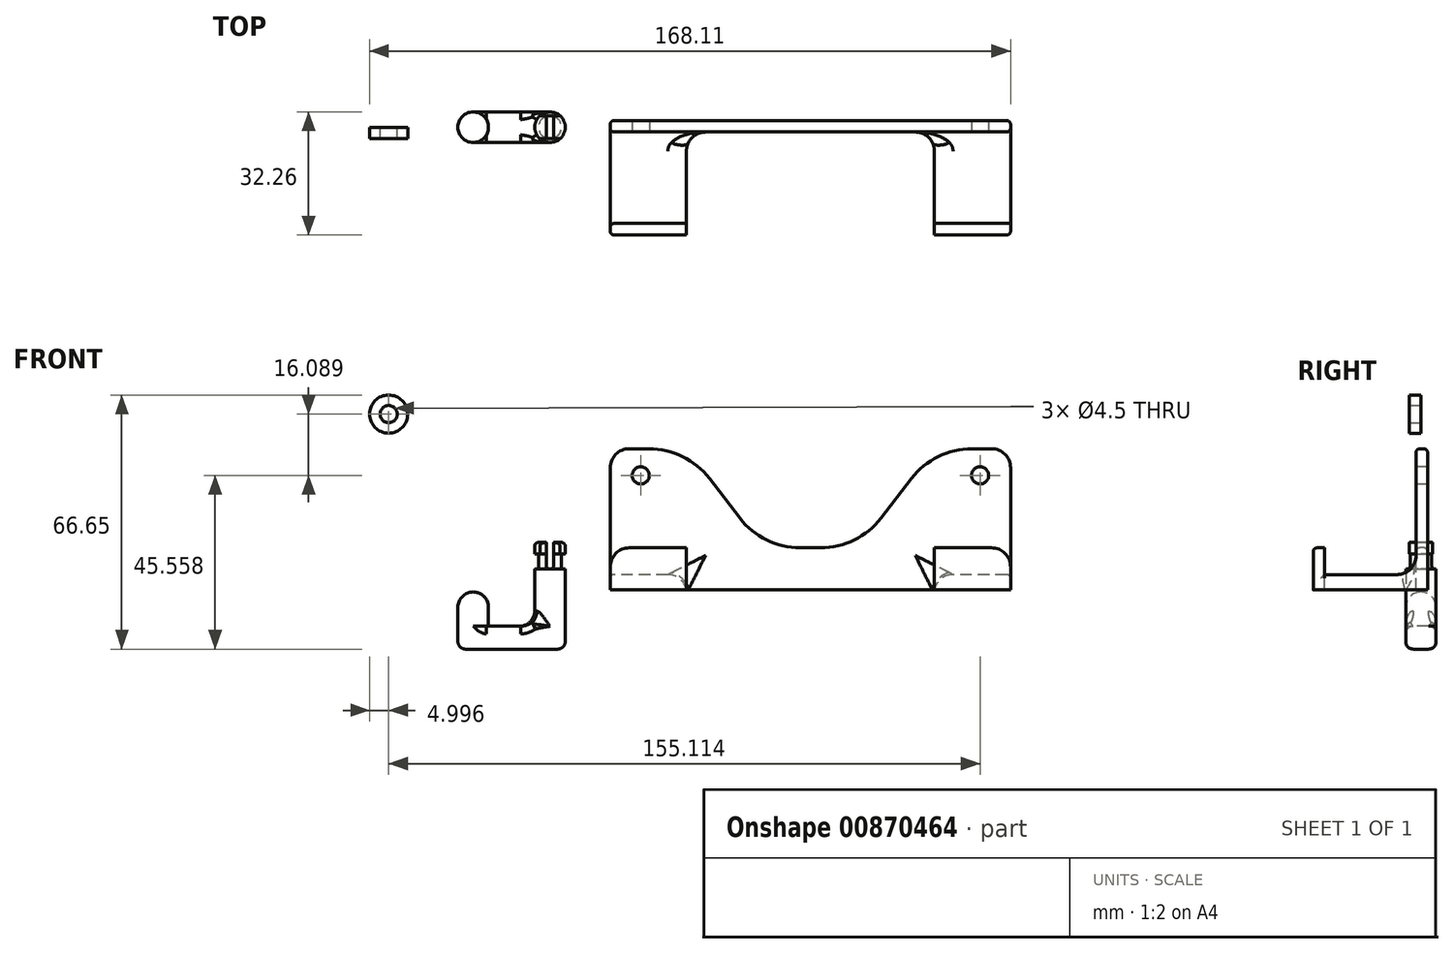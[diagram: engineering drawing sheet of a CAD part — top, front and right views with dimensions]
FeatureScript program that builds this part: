
annotation { "Feature Type Name" : "Feature", "Feature Type Description" : "" }
export const myFeature = defineFeature(function(context is Context, id is Id, definition is map)
    precondition{}
    {
        {
            var Q0;
            Q0=qCreatedBy(makeId("Right.planeOp"),FACE);
            var sketch = newSketch(context, id + "F0", { "sketchPlane" : qUnion([Q0])});
            skLineSegment(sketch, "E0", {"start": v(1.74, 52.56) * mm, "end": v(1.74, 15.56) * mm});
            skLineSegment(sketch, "E1", {"start": v(1.74, 15.56) * mm, "end": v(-28.26, 15.56) * mm});
            skLineSegment(sketch, "E2", {"start": v(-28.26, 15.56) * mm, "end": v(-28.26, 26.56) * mm});
            skLineSegment(sketch, "E3", {"start": v(-28.26, 26.56) * mm, "end": v(-25.26, 26.56) * mm});
            skLineSegment(sketch, "E4", {"start": v(-25.26, 26.56) * mm, "end": v(-25.26, 19.56) * mm});
            skLineSegment(sketch, "E5", {"start": v(-25.26, 19.56) * mm, "end": v(-1.26, 19.56) * mm});
            skLineSegment(sketch, "E6", {"start": v(-1.26, 19.56) * mm, "end": v(-1.26, 52.56) * mm});
            skLineSegment(sketch, "E7", {"start": v(-1.26, 52.56) * mm, "end": v(1.74, 52.56) * mm});
            skSolve(sketch);
        }
        {
            var Q0;
            Q0=makeQuery(id+"F0.imprint","IMPRINT",FACE,{"disambiguationData":[TD([[makeQuery(id+"F0.imprint","IMPRINT",EDGE,{"derivedFrom":sQuery(id+"F0.wireOp",EDGE,"E0")}),-1.0]])]});
            extrude(context, id + "F1", {"entities" : qUnion([Q0]), "depth" : 105 * mm, "offsetDistance" : 25 * mm});
        }
        {
            var Q0;
            Q0=makeQuery(id+"F1.opExtrude","SWEPT_FACE",FACE,{"disambiguationData":[OSD([sQuery(id+"F0.wireOp",EDGE,"E2")])]});
            var sketch = newSketch(context, id + "F2", { "sketchPlane" : qUnion([Q0])});
            skLineSegment(sketch, "E8", {"start": v(52.5, 106.7) * mm, "end": v(52.5, -58.22) * mm, "construction": true});
            skPoint(sketch, "E8.startSnap0", {"position": v(52.5, 26.56) * mm});
            skCircle(sketch, "E9", {"center": v(8, 45.56) * mm, "radius": 2.25 * mm});
            skCircle(sketch, "E10", {"center": v(97, 45.56) * mm, "radius": 2.25 * mm});
            skLineSegment(sketch, "E11.top", {"start": v(20, 15.56) * mm, "end": v(85, 15.56) * mm});
            skLineSegment(sketch, "E11.left", {"start": v(20, 26.56) * mm, "end": v(20, 15.56) * mm});
            skLineSegment(sketch, "E11.right", {"start": v(85, 26.56) * mm, "end": v(85, 15.56) * mm});
            skPoint(sketch, "E12.newPointA", {"position": v(105, 52.56) * mm});
            skPoint(sketch, "E12.newPointB", {"position": v(20, 52.56) * mm});
            skPoint(sketch, "E13.newPointA", {"position": v(40, 26.56) * mm});
            skPoint(sketch, "E14.0.end.orphan", {"position": v(0, 52.56) * mm});
            skLineSegment(sketch, "E15", {"start": v(26, 44.75) * mm, "end": v(34, 34.36) * mm});
            skLineSegment(sketch, "E16", {"start": v(71, 34.36) * mm, "end": v(79, 44.75) * mm});
            skLineSegment(sketch, "E17", {"start": v(85, 52.56) * mm, "end": v(20, 52.56) * mm});
            skLineSegment(sketch, "E18", {"start": v(49.85, 26.56) * mm, "end": v(55.15, 26.56) * mm});
            skArc(sketch, "E19.filletArc", {"start": v(34, 34.36) * mm, "mid": v(41.01, 28.62) * mm, "end": v(49.85, 26.56) * mm});
            skPoint(sketch, "E20.visualSharp", {"position": v(65, 26.56) * mm});
            skArc(sketch, "E20.filletArc", {"start": v(55.15, 26.56) * mm, "mid": v(63.99, 28.62) * mm, "end": v(71, 34.36) * mm});
            skLineSegment(sketch, "E21", {"start": v(10.15, 52.56) * mm, "end": v(0, 52.56) * mm});
            skLineSegment(sketch, "E22", {"start": v(94.85, 52.56) * mm, "end": v(105, 52.56) * mm});
            skArc(sketch, "E23.filletArc", {"start": v(26, 44.75) * mm, "mid": v(18.99, 50.5) * mm, "end": v(10.15, 52.56) * mm});
            skPoint(sketch, "E24.visualSharp", {"position": v(85, 52.56) * mm});
            skArc(sketch, "E24.filletArc", {"start": v(94.85, 52.56) * mm, "mid": v(86.01, 50.5) * mm, "end": v(79, 44.75) * mm});
            skLineSegment(sketch, "E25.0", {"start": v(105, 52.56) * mm, "end": v(0, 52.56) * mm});
            skSolve(sketch);
        }
        {
            var Q0;
            Q0=makeQuery(id+"F2.imprint","IMPRINT",FACE,{"disambiguationData":[TD([[makeQuery(id+"F2.imprint","IMPRINT",EDGE,{"derivedFrom":sQuery(id+"F2.wireOp",EDGE,"E9")}),1.0]])]});
            var Q1;
            Q1=makeQuery(id+"F2.imprint","IMPRINT",FACE,{"disambiguationData":[TD([[makeQuery(id+"F2.imprint","IMPRINT",EDGE,{"derivedFrom":sQuery(id+"F2.wireOp",EDGE,"E10")}),1.0]])]});
            var Q2;
            Q2=makeQuery(id+"F2.imprint","IMPRINT",FACE,{"disambiguationData":[TD([[makeQuery(id+"F2.imprint","IMPRINT",EDGE,{"derivedFrom":sQuery(id+"F2.wireOp",EDGE,"E15")}),1.0]])]});
            extrude(context, id + "F3", {"entities" : qUnion([Q0, Q1, Q2]), "operationType" : NewBodyOperationType.REMOVE, "endBound" : BoundingType.THROUGH_ALL, "oppositeDirection" : true, "depth" : 25 * mm, "offsetDistance" : 25 * mm});
        }
        {
            var Q0;
            Q0=makeQuery(id+"F2.imprint","IMPRINT",FACE,{"disambiguationData":[TD([[makeQuery(id+"F2.imprint","IMPRINT",EDGE,{"derivedFrom":sQuery(id+"F2.wireOp",EDGE,"E11.top")}),-1.0]])]});
            var Q1;
            Q1=makeQuery(id+"F1.opExtrude","SWEPT_FACE",FACE,{"disambiguationData":[OSD([sQuery(id+"F0.wireOp",EDGE,"E6")])]});
            extrude(context, id + "F4", {"entities" : qUnion([Q0]), "operationType" : NewBodyOperationType.REMOVE, "endBound" : BoundingType.UP_TO_SURFACE, "oppositeDirection" : true, "depth" : 25 * mm, "endBoundEntityFace" : qUnion([Q1]), "offsetDistance" : 25 * mm});
        }
        {
            var Q0;
            Q0=makeQuery(id+"F1.opExtrude","CAP_EDGE",EDGE,{"disambiguationData":[OSD([sQuery(id+"F0.wireOp",EDGE,"E7")])],"isStart":true});
            var Q1;
            Q1=makeQuery(id+"F1.opExtrude","CAP_EDGE",EDGE,{"disambiguationData":[OSD([sQuery(id+"F0.wireOp",EDGE,"E7")])],"isStart":false});
            var Q2;
            Q2=makeQuery(id+"F4.boolean.opBoolean","COPY",EDGE,{"derivedFrom":makeQuery(id+"F4.opExtrude","SWEPT_EDGE",EDGE,{"disambiguationData":[OSD([sQuery(id+"F0.wireOp",EDGE,"E2"),sQuery(id+"F0.wireOp",EDGE,"E3"),sQuery(id+"F2.wireOp",EDGE,"E11.right")])]})});
            var Q3;
            Q3=makeQuery(id+"F1.opExtrude","CAP_EDGE",EDGE,{"disambiguationData":[OSD([sQuery(id+"F0.wireOp",EDGE,"E3")])],"isStart":false});
            var Q4;
            Q4=makeQuery(id+"F1.opExtrude","CAP_EDGE",EDGE,{"disambiguationData":[OSD([sQuery(id+"F0.wireOp",EDGE,"E3")])],"isStart":true});
            var Q5;
            Q5=makeQuery(id+"F4.boolean.opBoolean","COPY",EDGE,{"derivedFrom":makeQuery(id+"F4.opExtrude","SWEPT_EDGE",EDGE,{"disambiguationData":[OSD([sQuery(id+"F0.wireOp",EDGE,"E2"),sQuery(id+"F0.wireOp",EDGE,"E3"),sQuery(id+"F2.wireOp",EDGE,"E11.left")])]})});
            var Q6;
            {var subQ0=sQuery(id+"F0.wireOp",EDGE,"E6");var subQ1=sQuery(id+"F2.wireOp",EDGE,"E11.right");var subQ4=sQuery(id+"F0.wireOp",EDGE,"E5");Q6=makeQuery(id+"F4.boolean.opBoolean","SPLIT",EDGE,{"disambiguationData":[TD([makeQuery(id+"F4.opExtrude","SWEPT_FACE",FACE,{"disambiguationData":[OSD([subQ1])]})])],"derivedFrom":makeQuery(id+"F1.opExtrude","SWEPT_EDGE",EDGE,{"disambiguationData":[OSD([subQ4,subQ0])]})});}
            var Q7;
            {var subQ0=sQuery(id+"F0.wireOp",EDGE,"E6");var subQ1=sQuery(id+"F2.wireOp",EDGE,"E11.left");var subQ4=sQuery(id+"F0.wireOp",EDGE,"E5");Q7=makeQuery(id+"F4.boolean.opBoolean","SPLIT",EDGE,{"disambiguationData":[TD([makeQuery(id+"F4.opExtrude","SWEPT_FACE",FACE,{"disambiguationData":[OSD([subQ1])]})])],"derivedFrom":makeQuery(id+"F1.opExtrude","SWEPT_EDGE",EDGE,{"disambiguationData":[OSD([subQ4,subQ0])]})});}
            var Q8;
            Q8=makeQuery(id+"F4.boolean.opBoolean","COPY",EDGE,{"derivedFrom":makeQuery(id+"F4.opExtrude","CAP_EDGE",EDGE,{"disambiguationData":[OSD([sQuery(id+"F2.wireOp",EDGE,"E11.right")])],"isStart":false})});
            var Q9;
            Q9=makeQuery(id+"F4.boolean.opBoolean","COPY",EDGE,{"derivedFrom":makeQuery(id+"F4.opExtrude","CAP_EDGE",EDGE,{"disambiguationData":[OSD([sQuery(id+"F2.wireOp",EDGE,"E11.left")])],"isStart":false})});
            fillet(context, id + "F5", {"entities" : qUnion([Q0, Q1, Q2, Q3, Q4, Q5, Q6, Q7, Q8, Q9]), "radius" : 5 * mm, "tangentPropagation" : true, "allowEdgeOverflow" : false});
        }
        {
            var Q0;
            Q0=makeQuery(id+"F4.boolean.opBoolean","INTERSECT",EDGE,{"derivedFrom":[makeQuery(id+"F1.opExtrude","SWEPT_FACE",FACE,{"disambiguationData":[OSD([sQuery(id+"F0.wireOp",EDGE,"E5")])]}),makeQuery(id+"F4.opExtrude","SWEPT_FACE",FACE,{"disambiguationData":[OSD([sQuery(id+"F2.wireOp",EDGE,"E11.right")])]})]});
            var Q1;
            Q1=makeQuery(id+"F4.boolean.opBoolean","INTERSECT",EDGE,{"derivedFrom":[makeQuery(id+"F1.opExtrude","SWEPT_FACE",FACE,{"disambiguationData":[OSD([sQuery(id+"F0.wireOp",EDGE,"E5")])]}),makeQuery(id+"F4.opExtrude","SWEPT_FACE",FACE,{"disambiguationData":[OSD([sQuery(id+"F2.wireOp",EDGE,"E11.left")])]})]});
            fillet(context, id + "F6", {"entities" : qUnion([Q0, Q1]), "radius" : 5 * mm, "tangentPropagation" : true, "allowEdgeOverflow" : false});
        }
        {
            var Q0;
            Q0=makeQuery(id+"F3.boolean.opBoolean","INTERSECT",EDGE,{"derivedFrom":[makeQuery(id+"F1.opExtrude","SWEPT_FACE",FACE,{"disambiguationData":[OSD([sQuery(id+"F0.wireOp",EDGE,"E6")])]}),makeQuery(id+"F3.opExtrude","SWEPT_FACE",FACE,{"disambiguationData":[OSD([sQuery(id+"F2.wireOp",EDGE,"E18")])]})]});
            var Q1;
            Q1=makeQuery(id+"F3.boolean.opBoolean","INTERSECT",EDGE,{"derivedFrom":[makeQuery(id+"F1.opExtrude","SWEPT_FACE",FACE,{"disambiguationData":[OSD([sQuery(id+"F0.wireOp",EDGE,"E0")])]}),makeQuery(id+"F3.opExtrude","SWEPT_FACE",FACE,{"disambiguationData":[OSD([sQuery(id+"F2.wireOp",EDGE,"E18")])]})]});
            var Q2;
            {var subQ0=sQuery(id+"F0.wireOp",EDGE,"E4");var subQ1=sQuery(id+"F0.wireOp",EDGE,"E3");Q2=makeQuery(id+"F4.boolean.opBoolean","SPLIT",EDGE,{"disambiguationData":[TD([makeQuery(id+"F4.opExtrude","SWEPT_FACE",FACE,{"disambiguationData":[OSD([sQuery(id+"F2.wireOp",EDGE,"E11.left")])]})])],"derivedFrom":makeQuery(id+"F1.opExtrude","SWEPT_EDGE",EDGE,{"disambiguationData":[OSD([subQ1,subQ0])]})});}
            var Q3;
            {var subQ0=sQuery(id+"F0.wireOp",EDGE,"E3");var subQ1=sQuery(id+"F0.wireOp",EDGE,"E2");Q3=makeQuery(id+"F4.boolean.opBoolean","SPLIT",EDGE,{"disambiguationData":[TD([makeQuery(id+"F4.opExtrude","SWEPT_FACE",FACE,{"disambiguationData":[OSD([sQuery(id+"F2.wireOp",EDGE,"E11.left")])]})])],"derivedFrom":makeQuery(id+"F1.opExtrude","SWEPT_EDGE",EDGE,{"disambiguationData":[OSD([subQ1,subQ0])]})});}
            var Q4;
            {var subQ0=sQuery(id+"F0.wireOp",EDGE,"E3");var subQ1=sQuery(id+"F0.wireOp",EDGE,"E2");Q4=makeQuery(id+"F4.boolean.opBoolean","SPLIT",EDGE,{"disambiguationData":[TD([makeQuery(id+"F4.opExtrude","SWEPT_FACE",FACE,{"disambiguationData":[OSD([sQuery(id+"F2.wireOp",EDGE,"E11.right")])]})])],"derivedFrom":makeQuery(id+"F1.opExtrude","SWEPT_EDGE",EDGE,{"disambiguationData":[OSD([subQ1,subQ0])]})});}
            var Q5;
            {var subQ1=sQuery(id+"F0.wireOp",EDGE,"E4");var subQ2=sQuery(id+"F0.wireOp",EDGE,"E3");var subQ3=sQuery(id+"F0.wireOp",EDGE,"E2");var subQ4=sQuery(id+"F2.wireOp",EDGE,"E11.right");Q5=makeQuery(id+"F5.opFillet","BLEND_EDGE",EDGE,{"blendedFrom":[makeQuery(id+"F4.boolean.opBoolean","COPY",EDGE,{"derivedFrom":makeQuery(id+"F4.opExtrude","SWEPT_EDGE",EDGE,{"disambiguationData":[OSD([subQ3,subQ2,subQ4])]})}),makeQuery(id+"F4.boolean.opBoolean","SPLIT",FACE,{"disambiguationData":[TD([makeQuery(id+"F4.opExtrude","SWEPT_FACE",FACE,{"disambiguationData":[OSD([subQ4])]})])],"derivedFrom":makeQuery(id+"F1.opExtrude","SWEPT_FACE",FACE,{"disambiguationData":[OSD([subQ1])]})})],"blendedInto":[makeQuery(id+"F4.boolean.opBoolean","SPLIT",FACE,{"disambiguationData":[TD([makeQuery(id+"F4.opExtrude","SWEPT_FACE",FACE,{"disambiguationData":[OSD([subQ4])]})])],"derivedFrom":makeQuery(id+"F1.opExtrude","SWEPT_FACE",FACE,{"disambiguationData":[OSD([subQ1])]})})]});}
            fillet(context, id + "F7", {"entities" : qUnion([Q0, Q1, Q2, Q3, Q4, Q5]), "radius" : 1 * mm, "tangentPropagation" : true, "allowEdgeOverflow" : false});
        }
        {
            var Q0;
            Q0=qCreatedBy(makeId("Top.planeOp"),FACE);
            var sketch = newSketch(context, id + "F8", { "sketchPlane" : qUnion([Q0])});
            skCircle(sketch, "E26", {"center": v(-15.8, 0) * mm, "radius": 4 * mm});
            skCircle(sketch, "E27", {"center": v(-35.94, 0) * mm, "radius": 4 * mm});
            skLineSegment(sketch, "E28", {"start": v(-35.94, -4) * mm, "end": v(-15.8, -4) * mm});
            skLineSegment(sketch, "E29", {"start": v(-15.8, 4) * mm, "end": v(-35.94, 4) * mm});
            skCircle(sketch, "E30", {"center": v(-15.8, 0) * mm, "radius": 3 * mm});
            skSolve(sketch);
        }
        {
            var Q0;
            {var subQ0=sQuery(id+"F8.wireOp",EDGE,"E27");var subQ1=makeQuery(id+"F8.imprint","INTERSECT",VERTEX,{"derivedFrom":[subQ0,sQuery(id+"F8.wireOp",EDGE,"E28")]});Q0=makeQuery(id+"F8.imprint","IMPRINT",FACE,{"disambiguationData":[TD([[makeQuery(id+"F8.imprint","IMPRINT",EDGE,{"disambiguationData":[TD([[subQ1,1.0]])],"derivedFrom":subQ0}),1.0]])]});}
            extrude(context, id + "F9", {"entities" : qUnion([Q0]), "depth" : 15 * mm, "offsetDistance" : 25 * mm});
        }
        {
            var Q0;
            Q0=makeQuery(id+"F8.imprint","IMPRINT",FACE,{"disambiguationData":[TD([[makeQuery(id+"F8.imprint","IMPRINT",EDGE,{"derivedFrom":sQuery(id+"F8.wireOp",EDGE,"E30")}),1.0]])]});
            var Q1;
            Q1=makeQuery(id+"F8.imprint","IMPRINT",FACE,{"disambiguationData":[TD([[makeQuery(id+"F8.imprint","IMPRINT",EDGE,{"derivedFrom":sQuery(id+"F8.wireOp",EDGE,"E30")}),-1.0]])]});
            var Q2;
            {var subQ0=sQuery(id+"F8.wireOp",EDGE,"E28");Q2=makeQuery(id+"F8.imprint","IMPRINT",FACE,{"disambiguationData":[TD([[makeQuery(id+"F8.imprint","IMPRINT",EDGE,{"derivedFrom":subQ0}),1.0]])]});}
            extrude(context, id + "F10", {"entities" : qUnion([Q0, Q1, Q2]), "operationType" : NewBodyOperationType.ADD, "depth" : 6 * mm, "offsetDistance" : 25 * mm});
        }
        {
            var Q0;
            Q0=makeQuery(id+"F8.imprint","IMPRINT",FACE,{"disambiguationData":[TD([[makeQuery(id+"F8.imprint","IMPRINT",EDGE,{"derivedFrom":sQuery(id+"F8.wireOp",EDGE,"E30")}),1.0]])]});
            var Q1;
            Q1=makeQuery(id+"F8.imprint","IMPRINT",FACE,{"disambiguationData":[TD([[makeQuery(id+"F8.imprint","IMPRINT",EDGE,{"derivedFrom":sQuery(id+"F8.wireOp",EDGE,"E30")}),-1.0]])]});
            extrude(context, id + "F11", {"entities" : qUnion([Q0, Q1]), "operationType" : NewBodyOperationType.ADD, "depth" : 28 * mm, "offsetDistance" : 25 * mm});
        }
        {
            var Q0;
            Q0=makeQuery(id+"F8.imprint","IMPRINT",FACE,{"disambiguationData":[TD([[makeQuery(id+"F8.imprint","IMPRINT",EDGE,{"derivedFrom":sQuery(id+"F8.wireOp",EDGE,"E30")}),-1.0]])]});
            extrude(context, id + "F12", {"entities" : qUnion([Q0]), "operationType" : NewBodyOperationType.REMOVE, "depth" : 25 * mm, "offsetDistance" : 25 * mm, "hasSecondDirection" : true, "secondDirectionOppositeDirection" : false, "secondDirectionDepth" : 21 * mm});
        }
        {
            var Q0;
            Q0=makeQuery(id+"F11.opExtrude","CAP_FACE",FACE,{"disambiguationData":[OSD([sQuery(id+"F8.wireOp",EDGE,"E26")])],"isStart":false});
            var sketch = newSketch(context, id + "F13", { "sketchPlane" : qUnion([Q0])});
            skLineSegment(sketch, "E31", {"start": v(-15.8, 29.3) * mm, "end": v(-15.8, -9.23) * mm, "construction": true});
            skLineSegment(sketch, "E32", {"start": v(-8.26, 0) * mm, "end": v(-53.8, 0) * mm, "construction": true});
            skLineSegment(sketch, "E33.bottom", {"start": v(-16.8, 6.08) * mm, "end": v(-14.8, 6.08) * mm});
            skLineSegment(sketch, "E33.top", {"start": v(-16.8, -7.23) * mm, "end": v(-14.8, -7.23) * mm});
            skLineSegment(sketch, "E33.left", {"start": v(-16.8, 6.08) * mm, "end": v(-16.8, -7.23) * mm});
            skLineSegment(sketch, "E33.right", {"start": v(-14.8, 6.08) * mm, "end": v(-14.8, -7.23) * mm});
            skLineSegment(sketch, "E34.bottom", {"start": v(-21.19, 4.55) * mm, "end": v(-9.3, 4.55) * mm});
            skLineSegment(sketch, "E34.top", {"start": v(-21.19, 3) * mm, "end": v(-9.3, 3) * mm});
            skLineSegment(sketch, "E34.left", {"start": v(-21.19, 4.55) * mm, "end": v(-21.19, 3) * mm});
            skLineSegment(sketch, "E34.right", {"start": v(-9.3, 4.55) * mm, "end": v(-9.3, 3) * mm});
            skLineSegment(sketch, "E35.bottom", {"start": v(-21.19, -6.06) * mm, "end": v(-9.07, -6.06) * mm});
            skLineSegment(sketch, "E35.top", {"start": v(-21.19, -3) * mm, "end": v(-9.07, -3) * mm});
            skLineSegment(sketch, "E35.left", {"start": v(-21.19, -6.06) * mm, "end": v(-21.19, -3) * mm});
            skLineSegment(sketch, "E35.right", {"start": v(-9.07, -6.06) * mm, "end": v(-9.07, -3) * mm});
            skSolve(sketch);
        }
        {
            var Q0;
            {var subQ0=sQuery(id+"F13.wireOp",EDGE,"ln6uyzeO-vsmx-rn3P-acM0-f8EmxYZYzspw.left");var subQ1=sQuery(id+"F13.wireOp",EDGE,"qbeKx2qP-LrLk-Yy0b-7lcU-67xgwiWYBIU2.bottom");var subQ2=makeQuery(id+"F13.imprint","INTERSECT",VERTEX,{"derivedFrom":[subQ1,subQ0]});Q0=makeQuery(id+"F13.imprint","IMPRINT",FACE,{"disambiguationData":[TD([[makeQuery(id+"F13.imprint","IMPRINT",EDGE,{"disambiguationData":[TD([[subQ2,-1.0]])],"derivedFrom":subQ1}),1.0]])]});}
            var Q1;
            {var subQ0=sQuery(id+"F13.wireOp",EDGE,"UMEJGvHE-ukJ3-Tcu8-njH4-oKaGY4YRu2tl.left");var subQ1=sQuery(id+"F13.wireOp",EDGE,"qbeKx2qP-LrLk-Yy0b-7lcU-67xgwiWYBIU2.bottom");var subQ2=makeQuery(id+"F13.imprint","INTERSECT",VERTEX,{"derivedFrom":[subQ1,subQ0]});Q1=makeQuery(id+"F13.imprint","IMPRINT",FACE,{"disambiguationData":[TD([[makeQuery(id+"F13.imprint","IMPRINT",EDGE,{"disambiguationData":[TD([[subQ2,-1.0]])],"derivedFrom":subQ1}),1.0]])]});}
            var Q2;
            {var subQ0=sQuery(id+"F13.wireOp",EDGE,"ln6uyzeO-vsmx-rn3P-acM0-f8EmxYZYzspw.left");var subQ1=sQuery(id+"F13.wireOp",EDGE,"qbeKx2qP-LrLk-Yy0b-7lcU-67xgwiWYBIU2.bottom");var subQ2=makeQuery(id+"F13.imprint","INTERSECT",VERTEX,{"derivedFrom":[subQ1,subQ0]});Q2=makeQuery(id+"F13.imprint","IMPRINT",FACE,{"disambiguationData":[TD([[makeQuery(id+"F13.imprint","IMPRINT",EDGE,{"disambiguationData":[TD([[subQ2,1.0]])],"derivedFrom":subQ1}),1.0]])]});}
            var Q3;
            {var subQ0=sQuery(id+"F13.wireOp",EDGE,"E34.top");var subQ1=sQuery(id+"F13.wireOp",EDGE,"E33.left");var subQ2=makeQuery(id+"F13.imprint","INTERSECT",VERTEX,{"derivedFrom":[subQ1,subQ0]});Q3=makeQuery(id+"F13.imprint","IMPRINT",FACE,{"disambiguationData":[TD([[makeQuery(id+"F13.imprint","IMPRINT",EDGE,{"disambiguationData":[TD([[subQ2,1.0]])],"derivedFrom":subQ1}),1.0]])]});}
            var Q4;
            {var subQ0=sQuery(id+"F13.wireOp",EDGE,"E34.top");var subQ1=sQuery(id+"F13.wireOp",EDGE,"E33.left");var subQ2=makeQuery(id+"F13.imprint","INTERSECT",VERTEX,{"derivedFrom":[subQ1,subQ0]});Q4=makeQuery(id+"F13.imprint","IMPRINT",FACE,{"disambiguationData":[TD([[makeQuery(id+"F13.imprint","IMPRINT",EDGE,{"disambiguationData":[TD([[subQ2,-1.0]])],"derivedFrom":subQ1}),1.0]])]});}
            var Q5;
            {var subQ0=sQuery(id+"F13.wireOp",EDGE,"E35.top");var subQ1=sQuery(id+"F13.wireOp",EDGE,"E33.left");var subQ2=makeQuery(id+"F13.imprint","INTERSECT",VERTEX,{"derivedFrom":[subQ1,subQ0]});Q5=makeQuery(id+"F13.imprint","IMPRINT",FACE,{"disambiguationData":[TD([[makeQuery(id+"F13.imprint","IMPRINT",EDGE,{"disambiguationData":[TD([[subQ2,-1.0]])],"derivedFrom":subQ1}),1.0]])]});}
            extrude(context, id + "F14", {"entities" : qUnion([Q0, Q1, Q2, Q3, Q4, Q5]), "operationType" : NewBodyOperationType.REMOVE, "oppositeDirection" : true, "depth" : 7 * mm, "offsetDistance" : 25 * mm});
        }
        {
            var Q0;
            {var subQ1=sQuery(id+"F13.wireOp",EDGE,"qbeKx2qP-LrLk-Yy0b-7lcU-67xgwiWYBIU2.left");Q0=makeQuery(id+"F13.imprint","IMPRINT",FACE,{"disambiguationData":[TD([[makeQuery(id+"F13.imprint","IMPRINT",EDGE,{"derivedFrom":subQ1}),1.0]])]});}
            var Q1;
            {var subQ0=sQuery(id+"F13.wireOp",EDGE,"UMEJGvHE-ukJ3-Tcu8-njH4-oKaGY4YRu2tl.left");var subQ1=sQuery(id+"F13.wireOp",EDGE,"qbeKx2qP-LrLk-Yy0b-7lcU-67xgwiWYBIU2.top");var subQ2=makeQuery(id+"F13.imprint","INTERSECT",VERTEX,{"derivedFrom":[subQ1,subQ0]});Q1=makeQuery(id+"F13.imprint","IMPRINT",FACE,{"disambiguationData":[TD([[makeQuery(id+"F13.imprint","IMPRINT",EDGE,{"disambiguationData":[TD([[subQ2,-1.0]])],"derivedFrom":subQ1}),1.0]])]});}
            var Q2;
            {var subQ0=sQuery(id+"F13.wireOp",EDGE,"E34.top");var subQ1=sQuery(id+"F13.wireOp",EDGE,"E33.left");var subQ2=makeQuery(id+"F13.imprint","INTERSECT",VERTEX,{"derivedFrom":[subQ1,subQ0]});Q2=makeQuery(id+"F13.imprint","IMPRINT",FACE,{"disambiguationData":[TD([[makeQuery(id+"F13.imprint","IMPRINT",EDGE,{"disambiguationData":[TD([[subQ2,1.0]])],"derivedFrom":subQ1}),-1.0]])]});}
            var Q3;
            {var subQ0=sQuery(id+"F13.wireOp",EDGE,"E34.top");var subQ1=sQuery(id+"F13.wireOp",EDGE,"E33.right");var subQ2=makeQuery(id+"F13.imprint","INTERSECT",VERTEX,{"derivedFrom":[subQ1,subQ0]});Q3=makeQuery(id+"F13.imprint","IMPRINT",FACE,{"disambiguationData":[TD([[makeQuery(id+"F13.imprint","IMPRINT",EDGE,{"disambiguationData":[TD([[subQ2,1.0]])],"derivedFrom":subQ1}),1.0]])]});}
            var Q4;
            {var subQ0=sQuery(id+"F13.wireOp",EDGE,"E35.top");var subQ1=sQuery(id+"F13.wireOp",EDGE,"E33.left");var subQ2=makeQuery(id+"F13.imprint","INTERSECT",VERTEX,{"derivedFrom":[subQ1,subQ0]});Q4=makeQuery(id+"F13.imprint","IMPRINT",FACE,{"disambiguationData":[TD([[makeQuery(id+"F13.imprint","IMPRINT",EDGE,{"disambiguationData":[TD([[subQ2,-1.0]])],"derivedFrom":subQ1}),-1.0]])]});}
            var Q5;
            {var subQ0=sQuery(id+"F13.wireOp",EDGE,"E35.top");var subQ1=sQuery(id+"F13.wireOp",EDGE,"E33.right");var subQ2=makeQuery(id+"F13.imprint","INTERSECT",VERTEX,{"derivedFrom":[subQ1,subQ0]});Q5=makeQuery(id+"F13.imprint","IMPRINT",FACE,{"disambiguationData":[TD([[makeQuery(id+"F13.imprint","IMPRINT",EDGE,{"disambiguationData":[TD([[subQ2,-1.0]])],"derivedFrom":subQ1}),1.0]])]});}
            var Q6;
            {var subQ0=sQuery(id+"F13.wireOp",EDGE,"E33.bottom");Q6=makeQuery(id+"F13.imprint","IMPRINT",FACE,{"disambiguationData":[TD([[makeQuery(id+"F13.imprint","IMPRINT",EDGE,{"derivedFrom":subQ0}),-1.0]])]});}
            extrude(context, id + "F15", {"entities" : qUnion([Q0, Q1, Q2, Q3, Q4, Q5, Q6]), "operationType" : NewBodyOperationType.REMOVE, "oppositeDirection" : true, "depth" : 5 * mm, "offsetDistance" : 25 * mm});
        }
        {
            var Q0;
            Q0=makeQuery(id+"F9.opExtrude","CAP_EDGE",EDGE,{"disambiguationData":[OSD([sQuery(id+"F8.wireOp",EDGE,"E27")])],"isStart":false});
            var Q1;
            Q1=makeQuery(id+"F10.opExtrude","CAP_EDGE",EDGE,{"disambiguationData":[OSD([sQuery(id+"F8.wireOp",EDGE,"E27")])],"isStart":false});
            var Q2;
            {var subQ0=sQuery(id+"F8.wireOp",EDGE,"E26");Q2=makeQuery(id+"F11.boolean.opBoolean","INTERSECT",EDGE,{"derivedFrom":[makeQuery(id+"F10.opExtrude","CAP_FACE",FACE,{"disambiguationData":[OSD([subQ0,sQuery(id+"F8.wireOp",EDGE,"E27"),sQuery(id+"F8.wireOp",EDGE,"E28"),sQuery(id+"F8.wireOp",EDGE,"E29")])],"isStart":false}),makeQuery(id+"F11.opExtrude","SWEPT_FACE",FACE,{"disambiguationData":[OSD([subQ0])]})]});}
            fillet(context, id + "F16", {"entities" : qUnion([Q0, Q1, Q2]), "radius" : 4 * mm, "tangentPropagation" : true, "allowEdgeOverflow" : false});
        }
        {
            var Q0;
            {var subQ0=sQuery(id+"F8.wireOp",EDGE,"E26");Q0=makeQuery(id+"F14.boolean.opBoolean","SPLIT",EDGE,{"disambiguationData":[TD([makeQuery(id+"F14.opExtrude","SWEPT_FACE",FACE,{"disambiguationData":[OSD([sQuery(id+"F13.wireOp",EDGE,"J1QhrFvL-nhcP-Zsf0-0vtz-GyqxPvx9N3jh.left")])]})])],"derivedFrom":makeQuery(id+"F11.opExtrude","CAP_EDGE",EDGE,{"disambiguationData":[OSD([subQ0])],"isStart":false})});}
            var Q1;
            {var subQ0=sQuery(id+"F8.wireOp",EDGE,"E26");Q1=makeQuery(id+"F14.boolean.opBoolean","SPLIT",EDGE,{"disambiguationData":[TD([makeQuery(id+"F14.opExtrude","SWEPT_FACE",FACE,{"disambiguationData":[OSD([sQuery(id+"F13.wireOp",EDGE,"J1QhrFvL-nhcP-Zsf0-0vtz-GyqxPvx9N3jh.right")])]})])],"derivedFrom":makeQuery(id+"F11.opExtrude","CAP_EDGE",EDGE,{"disambiguationData":[OSD([subQ0])],"isStart":false})});}
            var Q2;
            Q2=makeQuery(id+"F10.opExtrude","CAP_EDGE",EDGE,{"disambiguationData":[OSD([sQuery(id+"F8.wireOp",EDGE,"E28")])],"isStart":false});
            var Q3;
            Q3=makeQuery(id+"F10.opExtrude","CAP_EDGE",EDGE,{"disambiguationData":[OSD([sQuery(id+"F8.wireOp",EDGE,"E29")])],"isStart":false});
            var Q4;
            {var subQ0=sQuery(id+"F8.wireOp",EDGE,"E27");Q4=makeQuery(id+"F10.boolean.opBoolean","MERGE",FACE,{"derivedFrom":[makeQuery(id+"F9.opExtrude","CAP_FACE",FACE,{"disambiguationData":[OSD([subQ0])],"isStart":true}),makeQuery(id+"F10.opExtrude","CAP_FACE",FACE,{"disambiguationData":[OSD([sQuery(id+"F8.wireOp",EDGE,"E26"),subQ0,sQuery(id+"F8.wireOp",EDGE,"E28"),sQuery(id+"F8.wireOp",EDGE,"E29")])],"isStart":true})]});}
            fillet(context, id + "F17", {"entities" : qUnion([Q0, Q1, Q2, Q3, Q4]), "radius" : 2 * mm, "tangentPropagation" : true, "allowEdgeOverflow" : false});
        }
        {
            var Q0;
            {var subQ0=sQuery(id+"F8.wireOp",EDGE,"E26");Q0=makeQuery(id+"F14.boolean.opBoolean","SPLIT",EDGE,{"disambiguationData":[TD([makeQuery(id+"F14.opExtrude","SWEPT_FACE",FACE,{"disambiguationData":[OSD([sQuery(id+"F13.wireOp",EDGE,"qbeKx2qP-LrLk-Yy0b-7lcU-67xgwiWYBIU2.bottom")])]})])],"derivedFrom":makeQuery(id+"F11.opExtrude","CAP_EDGE",EDGE,{"disambiguationData":[OSD([subQ0])],"isStart":false})});}
            var Q1;
            {var subQ0=sQuery(id+"F8.wireOp",EDGE,"E26");Q1=makeQuery(id+"F14.boolean.opBoolean","SPLIT",EDGE,{"disambiguationData":[TD([makeQuery(id+"F14.opExtrude","SWEPT_FACE",FACE,{"disambiguationData":[OSD([sQuery(id+"F13.wireOp",EDGE,"qbeKx2qP-LrLk-Yy0b-7lcU-67xgwiWYBIU2.top")])]})])],"derivedFrom":makeQuery(id+"F11.opExtrude","CAP_EDGE",EDGE,{"disambiguationData":[OSD([subQ0])],"isStart":false})});}
            var Q2;
            {var subQ0=sQuery(id+"F13.wireOp",EDGE,"ln6uyzeO-vsmx-rn3P-acM0-f8EmxYZYzspw.left");var subQ1=sQuery(id+"F8.wireOp",EDGE,"E26");var subQ3=sQuery(id+"F13.wireOp",EDGE,"qbeKx2qP-LrLk-Yy0b-7lcU-67xgwiWYBIU2.top");var subQ4=makeQuery(id+"F11.opExtrude","CAP_FACE",FACE,{"disambiguationData":[OSD([subQ1])],"isStart":false});Q2=makeQuery(id+"F15.boolean.opBoolean","INTERSECT",EDGE,{"derivedFrom":[makeQuery(id+"F14.boolean.opBoolean","SPLIT",FACE,{"disambiguationData":[TD([makeQuery(id+"F14.opExtrude","SWEPT_FACE",FACE,{"disambiguationData":[OSD([subQ3])]})])],"derivedFrom":makeQuery(id+"F12.boolean.opBoolean","SPLIT",FACE,{"disambiguationData":[TD([subQ4])],"derivedFrom":makeQuery(id+"F11.boolean.opBoolean","MERGE",FACE,{"derivedFrom":[makeQuery(id+"F10.opExtrude","SWEPT_FACE",FACE,{"disambiguationData":[OSD([subQ1])]}),makeQuery(id+"F11.opExtrude","SWEPT_FACE",FACE,{"disambiguationData":[OSD([subQ1])]})]})})}),makeQuery(id+"F15.opExtrude","SWEPT_FACE",FACE,{"disambiguationData":[OSD([subQ0]),TDD([makeQuery(id+"F13.imprint","IMPRINT",EDGE,{"disambiguationData":[TD([[makeQuery(id+"F13.imprint","INTERSECT",VERTEX,{"derivedFrom":[subQ3,subQ0]}),-1.0]])],"derivedFrom":subQ0}),makeQuery(id+"F13.imprint","IMPRINT",EDGE,{"disambiguationData":[TD([[makeQuery(id+"F13.imprint","INTERSECT",VERTEX,{"derivedFrom":[sQuery(id+"F13.wireOp",EDGE,"ln6uyzeO-vsmx-rn3P-acM0-f8EmxYZYzspw.top"),subQ0]}),1.0]])],"derivedFrom":subQ0})])]})]});}
            var Q3;
            {var subQ0=sQuery(id+"F13.wireOp",EDGE,"UMEJGvHE-ukJ3-Tcu8-njH4-oKaGY4YRu2tl.left");var subQ1=sQuery(id+"F8.wireOp",EDGE,"E26");var subQ3=sQuery(id+"F13.wireOp",EDGE,"qbeKx2qP-LrLk-Yy0b-7lcU-67xgwiWYBIU2.top");var subQ4=makeQuery(id+"F11.opExtrude","CAP_FACE",FACE,{"disambiguationData":[OSD([subQ1])],"isStart":false});Q3=makeQuery(id+"F15.boolean.opBoolean","INTERSECT",EDGE,{"derivedFrom":[makeQuery(id+"F14.boolean.opBoolean","SPLIT",FACE,{"disambiguationData":[TD([makeQuery(id+"F14.opExtrude","SWEPT_FACE",FACE,{"disambiguationData":[OSD([subQ3])]})])],"derivedFrom":makeQuery(id+"F12.boolean.opBoolean","SPLIT",FACE,{"disambiguationData":[TD([subQ4])],"derivedFrom":makeQuery(id+"F11.boolean.opBoolean","MERGE",FACE,{"derivedFrom":[makeQuery(id+"F10.opExtrude","SWEPT_FACE",FACE,{"disambiguationData":[OSD([subQ1])]}),makeQuery(id+"F11.opExtrude","SWEPT_FACE",FACE,{"disambiguationData":[OSD([subQ1])]})]})})}),makeQuery(id+"F15.opExtrude","SWEPT_FACE",FACE,{"disambiguationData":[OSD([subQ0]),TDD([makeQuery(id+"F13.imprint","IMPRINT",EDGE,{"disambiguationData":[TD([[makeQuery(id+"F13.imprint","INTERSECT",VERTEX,{"derivedFrom":[subQ3,subQ0]}),-1.0]])],"derivedFrom":subQ0}),makeQuery(id+"F13.imprint","IMPRINT",EDGE,{"disambiguationData":[TD([[makeQuery(id+"F13.imprint","INTERSECT",VERTEX,{"derivedFrom":[sQuery(id+"F13.wireOp",EDGE,"UMEJGvHE-ukJ3-Tcu8-njH4-oKaGY4YRu2tl.top"),subQ0]}),1.0]])],"derivedFrom":subQ0})])]})]});}
            var Q4;
            {var subQ0=sQuery(id+"F13.wireOp",EDGE,"UMEJGvHE-ukJ3-Tcu8-njH4-oKaGY4YRu2tl.left");var subQ1=sQuery(id+"F13.wireOp",EDGE,"qbeKx2qP-LrLk-Yy0b-7lcU-67xgwiWYBIU2.bottom");var subQ2=sQuery(id+"F8.wireOp",EDGE,"E26");var subQ4=makeQuery(id+"F11.opExtrude","CAP_FACE",FACE,{"disambiguationData":[OSD([subQ2])],"isStart":false});Q4=makeQuery(id+"F15.boolean.opBoolean","INTERSECT",EDGE,{"derivedFrom":[makeQuery(id+"F14.boolean.opBoolean","SPLIT",FACE,{"disambiguationData":[TD([makeQuery(id+"F14.opExtrude","SWEPT_FACE",FACE,{"disambiguationData":[OSD([subQ1])]})])],"derivedFrom":makeQuery(id+"F12.boolean.opBoolean","SPLIT",FACE,{"disambiguationData":[TD([subQ4])],"derivedFrom":makeQuery(id+"F11.boolean.opBoolean","MERGE",FACE,{"derivedFrom":[makeQuery(id+"F10.opExtrude","SWEPT_FACE",FACE,{"disambiguationData":[OSD([subQ2])]}),makeQuery(id+"F11.opExtrude","SWEPT_FACE",FACE,{"disambiguationData":[OSD([subQ2])]})]})})}),makeQuery(id+"F15.opExtrude","SWEPT_FACE",FACE,{"disambiguationData":[OSD([subQ0]),TDD([makeQuery(id+"F13.imprint","IMPRINT",EDGE,{"disambiguationData":[TD([[makeQuery(id+"F13.imprint","INTERSECT",VERTEX,{"derivedFrom":[sQuery(id+"F13.wireOp",EDGE,"UMEJGvHE-ukJ3-Tcu8-njH4-oKaGY4YRu2tl.bottom"),subQ0]}),-1.0]])],"derivedFrom":subQ0}),makeQuery(id+"F13.imprint","IMPRINT",EDGE,{"disambiguationData":[TD([[makeQuery(id+"F13.imprint","INTERSECT",VERTEX,{"derivedFrom":[subQ1,subQ0]}),1.0]])],"derivedFrom":subQ0})])]})]});}
            var Q5;
            {var subQ0=sQuery(id+"F13.wireOp",EDGE,"ln6uyzeO-vsmx-rn3P-acM0-f8EmxYZYzspw.left");var subQ1=sQuery(id+"F13.wireOp",EDGE,"qbeKx2qP-LrLk-Yy0b-7lcU-67xgwiWYBIU2.bottom");var subQ2=sQuery(id+"F8.wireOp",EDGE,"E26");var subQ4=makeQuery(id+"F11.opExtrude","CAP_FACE",FACE,{"disambiguationData":[OSD([subQ2])],"isStart":false});Q5=makeQuery(id+"F15.boolean.opBoolean","INTERSECT",EDGE,{"derivedFrom":[makeQuery(id+"F14.boolean.opBoolean","SPLIT",FACE,{"disambiguationData":[TD([makeQuery(id+"F14.opExtrude","SWEPT_FACE",FACE,{"disambiguationData":[OSD([subQ1])]})])],"derivedFrom":makeQuery(id+"F12.boolean.opBoolean","SPLIT",FACE,{"disambiguationData":[TD([subQ4])],"derivedFrom":makeQuery(id+"F11.boolean.opBoolean","MERGE",FACE,{"derivedFrom":[makeQuery(id+"F10.opExtrude","SWEPT_FACE",FACE,{"disambiguationData":[OSD([subQ2])]}),makeQuery(id+"F11.opExtrude","SWEPT_FACE",FACE,{"disambiguationData":[OSD([subQ2])]})]})})}),makeQuery(id+"F15.opExtrude","SWEPT_FACE",FACE,{"disambiguationData":[OSD([subQ0]),TDD([makeQuery(id+"F13.imprint","IMPRINT",EDGE,{"disambiguationData":[TD([[makeQuery(id+"F13.imprint","INTERSECT",VERTEX,{"derivedFrom":[sQuery(id+"F13.wireOp",EDGE,"ln6uyzeO-vsmx-rn3P-acM0-f8EmxYZYzspw.bottom"),subQ0]}),-1.0]])],"derivedFrom":subQ0}),makeQuery(id+"F13.imprint","IMPRINT",EDGE,{"disambiguationData":[TD([[makeQuery(id+"F13.imprint","INTERSECT",VERTEX,{"derivedFrom":[subQ1,subQ0]}),1.0]])],"derivedFrom":subQ0})])]})]});}
            var Q6;
            Q6=makeQuery(id+"F14.boolean.opBoolean","COPY",EDGE,{"derivedFrom":makeQuery(id+"F14.opExtrude","CAP_EDGE",EDGE,{"disambiguationData":[OSD([sQuery(id+"F13.wireOp",EDGE,"E33.left")])],"isStart":false})});
            var Q7;
            Q7=makeQuery(id+"F14.boolean.opBoolean","COPY",EDGE,{"derivedFrom":makeQuery(id+"F14.opExtrude","CAP_EDGE",EDGE,{"disambiguationData":[OSD([sQuery(id+"F13.wireOp",EDGE,"E33.right")])],"isStart":false})});
            var Q8;
            {var subQ0=sQuery(id+"F8.wireOp",EDGE,"E26");Q8=makeQuery(id+"F14.boolean.opBoolean","SPLIT",EDGE,{"disambiguationData":[TD([makeQuery(id+"F14.opExtrude","SWEPT_FACE",FACE,{"disambiguationData":[OSD([sQuery(id+"F13.wireOp",EDGE,"E33.left")])]})])],"derivedFrom":makeQuery(id+"F11.opExtrude","CAP_EDGE",EDGE,{"disambiguationData":[OSD([subQ0])],"isStart":false})});}
            var Q9;
            {var subQ0=sQuery(id+"F8.wireOp",EDGE,"E26");Q9=makeQuery(id+"F14.boolean.opBoolean","SPLIT",EDGE,{"disambiguationData":[TD([makeQuery(id+"F14.opExtrude","SWEPT_FACE",FACE,{"disambiguationData":[OSD([sQuery(id+"F13.wireOp",EDGE,"E33.right")])]})])],"derivedFrom":makeQuery(id+"F11.opExtrude","CAP_EDGE",EDGE,{"disambiguationData":[OSD([subQ0])],"isStart":false})});}
            fillet(context, id + "F18", {"entities" : qUnion([Q0, Q1, Q2, Q3, Q4, Q5, Q6, Q7, Q8, Q9]), "radius" : 1 * mm, "tangentPropagation" : true, "allowEdgeOverflow" : false});
        }
        {
            var Q0;
            Q0=qCreatedBy(makeId("Front.planeOp"),FACE);
            var sketch = newSketch(context, id + "F19", { "sketchPlane" : qUnion([Q0])});
            skCircle(sketch, "E36", {"center": v(-58.11, 61.65) * mm, "radius": 5 * mm});
            skCircle(sketch, "E37", {"center": v(-58.11, 61.65) * mm, "radius": 2.25 * mm});
            skSolve(sketch);
        }
        {
            var Q0;
            Q0=makeQuery(id+"F19.imprint","IMPRINT",FACE,{"disambiguationData":[TD([[makeQuery(id+"F19.imprint","IMPRINT",EDGE,{"derivedFrom":sQuery(id+"F19.wireOp",EDGE,"E36")}),1.0]])]});
            extrude(context, id + "F20", {"entities" : qUnion([Q0]), "depth" : 3 * mm, "offsetDistance" : 25 * mm});
        }
    });
